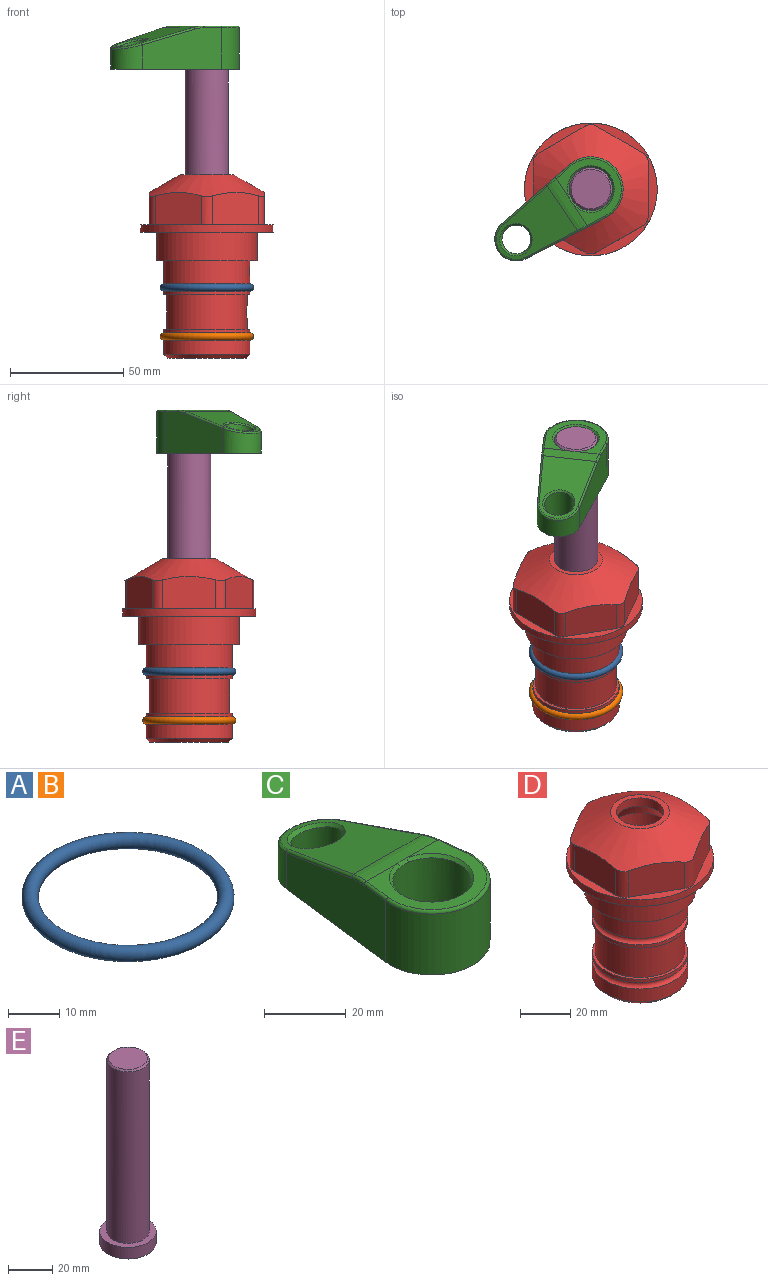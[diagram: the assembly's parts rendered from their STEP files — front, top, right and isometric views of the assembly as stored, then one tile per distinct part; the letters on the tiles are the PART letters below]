
ASSEMBLY  parts=5 mates=4
PART A: 1 faces, bbox 44.7x44.7x3.2 mm
  f0: torus R=19.05mm, axis (0,0,1), area 1193.9mm2
PART B: same geometry as A
PART C: 31 faces, bbox 31.7x65.5x19.8 mm
  f0: plane 39.12x18.26mm, normal (0.99,0.12,0), area 612.2mm2, adj f1,f4,f7,f11,f13,f15
  f1: cylinder r=9.53mm len=18.91mm, axis (0,0,-1), area 296.1mm2, adj f0,f2,f7,f17
  f2: plane 39.12x18.26mm, normal (-0.99,0.12,0), area 612.2mm2, adj f1,f4,f7,f12,f14,f16
  f3: cylinder r=6.35mm len=12.7mm, axis (0,0,-1), area 362.4mm2, adj f7,f18
  f4: cylinder r=14.29mm len=28.58mm, axis (0,0,-1), area 882.2mm2, adj f0,f2,f7,f10
  f5: cylinder r=9.53mm len=19.05mm, axis (0,0,-1), area 1092.6mm2, adj f7,f19,f20
  f6: plane 26.99x23.69mm, normal (0,0,1), area 216.2mm2, adj f9,f10,f11,f12,f19
  f7: plane 63.5x28.58mm, normal (0,0,-1), area 661.8mm2, adj f0,f1,f2,f3,f4,f5,f22,f23
  f8: plane 33.52x23.6mm, normal (0,0.26,0.97), area 486mm2, adj f9,f15,f16,f17,f18
  f9: cylinder r=19.05mm len=24.72mm, axis (1,0,0), area 120.4mm2, adj f6,f8,f13,f14,f20
  f10: torus R=13.49mm, axis (0,0,1), area 59mm2, adj f4,f6,f11,f12
  f11: cylinder r=0.79mm len=8.67mm, axis (0.12,-0.99,0), area 10.8mm2, adj f0,f6,f10,f13
  f12: cylinder r=0.79mm len=8.67mm, axis (0.12,0.99,0), area 10.8mm2, adj f2,f6,f10,f14
  f13: bspline ~4.95x1.42mm, area 6.1mm2, adj f0,f9,f11,f15
  f14: bspline ~4.95x1.42mm, area 6.1mm2, adj f2,f9,f12,f16
  f15: cylinder r=0.79mm len=25.95mm, axis (0.12,-0.96,0.26), area 32.9mm2, adj f0,f8,f13,f17
  f16: cylinder r=0.79mm len=25.95mm, axis (0.12,0.96,-0.26), area 32.9mm2, adj f2,f8,f14,f17
  f17: bspline ~18.91x8.38mm, area 30mm2, adj f1,f8,f15,f16
  f18: bspline ~14.29x14.29mm, area 48.3mm2, adj f3,f8
  f19: cone r=9.53mm half-angle=45deg, axis (0,0,1), area 66.5mm2, adj f5,f6,f20
  f20: bspline ~3.22x0.96mm, area 3.5mm2, adj f5,f9,f19
  f21: plane 2.75x2.72mm, normal (0,0,-1), area 2.9mm2, adj f23,f25,f28
  f22: plane 23.05x15.88mm, normal (-0.99,-0.12,0), area 323.6mm2, adj f7,f25,f26,f27,f28,f29
  f23: plane 23.05x15.88mm, normal (0.99,-0.12,0), area 323.6mm2, adj f7,f21,f25,f27,f28,f30
  f24: cylinder r=9.53mm len=10.69mm, axis (0,0,-1), area 114.7mm2, adj f7,f27,f29,f30
  f25: cylinder r=12.7mm len=20.59mm, axis (0,0,-1), area 381.1mm2, adj f7,f21,f22,f23,f26,f28
  f26: plane 2.75x2.72mm, normal (0,0,-1), area 2.9mm2, adj f22,f25,f28
  f27: plane 19.72x18.37mm, normal (0,-0.26,-0.97), area 291.8mm2, adj f22,f23,f24,f28,f29,f30
  f28: cylinder r=15.88mm len=19.92mm, axis (1,0,0), area 54.8mm2, adj f21,f22,f23,f25,f26,f27
  f29: cylinder r=1.59mm len=11mm, axis (0,0,-1), area 34.7mm2, adj f7,f22,f24,f27
  f30: cylinder r=1.59mm len=11mm, axis (0,0,-1), area 34.7mm2, adj f7,f23,f24,f27
PART D: 36 faces, bbox 58.7x58.7x81 mm
  f0: cylinder r=17.78mm len=35.56mm, axis (0,0,1), area 1670.8mm2, adj f23,f24,f31
  f1: cylinder r=19.05mm len=38.1mm, axis (0,0,1), area 1191.9mm2, adj f26,f27,f30
  f2: plane 58.66x58.66mm, normal (0,0,-1), area 1150.6mm2, adj f3,f28
  f3: cylinder r=29.33mm len=58.66mm, axis (0,0,-1), area 585.1mm2, adj f2,f4
  f4: plane 58.66x58.66mm, normal (0,0,1), area 475.9mm2, adj f3,f5,f6,f7,f8,f9,f10,f11
  f5: plane 20.32x14.34mm, normal (-0.5,0.87,0), area 324.4mm2, adj f4,f15,f16,f17
  f6: plane 20.32x14.34mm, normal (0.5,0.87,0), area 324.4mm2, adj f4,f14,f15,f17
  f7: plane 23.48x14.34mm, normal (1,0,0), area 324.4mm2, adj f4,f13,f14,f17
  f8: plane 20.32x14.34mm, normal (0.5,-0.87,0), area 324.4mm2, adj f4,f12,f13,f17
  f9: plane 20.32x14.34mm, normal (-0.5,-0.87,0), area 324.4mm2, adj f4,f11,f12,f17
  f10: plane 23.48x14.34mm, normal (-1,0,0), area 324.4mm2, adj f4,f11,f16,f17
  f11: cylinder r=5.08mm len=12.85mm, axis (0,0,-1), area 67.2mm2, adj f4,f9,f10,f17
  f12: cylinder r=5.08mm len=12.85mm, axis (0,0,-1), area 67.2mm2, adj f4,f8,f9,f17
  f13: cylinder r=5.08mm len=12.85mm, axis (0,0,-1), area 67.2mm2, adj f4,f7,f8,f17
  f14: cylinder r=5.08mm len=12.85mm, axis (0,0,-1), area 67.2mm2, adj f4,f6,f7,f17
  f15: cylinder r=5.08mm len=12.85mm, axis (0,0,-1), area 67.2mm2, adj f4,f5,f6,f17
  f16: cylinder r=5.08mm len=12.85mm, axis (0,0,-1), area 67.2mm2, adj f4,f5,f10,f17
  f17: cone r=11.73mm half-angle=60deg, axis (0,0,-1), area 2071.8mm2, adj f5,f6,f7,f8,f9,f10,f11,f12
  f18: plane 23.46x23.46mm, normal (0,0,1), area 147.4mm2, adj f17,f35
  f19: plane 34.93x34.93mm, normal (0,0,-1), area 958mm2, adj f29
  f20: cylinder r=19.05mm len=38.1mm, axis (0,0,1), area 760.1mm2, adj f21,f29
  f21: torus R=19.05mm, axis (0,0,1), area 565.3mm2, adj f20,f22
  f22: cylinder r=19.05mm len=38.1mm, axis (0,0,1), area 190mm2, adj f21,f23
  f23: plane 38.1x38.1mm, normal (0,0,1), area 146.9mm2, adj f0,f22
  f24: plane 38.1x38.1mm, normal (0,0,-1), area 146.9mm2, adj f0,f25
  f25: cylinder r=19.05mm len=38.1mm, axis (0,0,1), area 190mm2, adj f24,f26
  f26: torus R=19.05mm, axis (0,0,1), area 565.3mm2, adj f1,f25
  f27: plane 44.45x44.45mm, normal (0,0,-1), area 411.7mm2, adj f1,f28
  f28: cylinder r=22.23mm len=44.45mm, axis (0,0,1), area 1773.5mm2, adj f2,f27
  f29: cone r=19.05mm half-angle=45deg, axis (0,0,1), area 257.5mm2, adj f19,f20
  f30: cylinder r=3.17mm len=6.75mm, axis (-1,0,0), area 128mm2, adj f1,f33
  f31: cylinder r=3.17mm len=6.35mm, axis (-1,0,0), area 102.5mm2, adj f0,f33
  f32: plane 25.4x25.4mm, normal (0,0,1), area 506.7mm2, adj f33
  f33: cylinder r=12.7mm len=66.42mm, axis (0,0,-1), area 5236.2mm2, adj f30,f31,f32,f34
  f34: cone r=9.53mm half-angle=30deg, axis (0,0,-1), area 443.4mm2, adj f33,f35
  f35: cylinder r=9.53mm len=19.05mm, axis (0,0,-1), area 240.9mm2, adj f18,f34
PART E: 6 faces, bbox 25.4x25.4x101.6 mm
  f0: plane 17.46x17.46mm, normal (0,0,1), area 239.5mm2, adj f5
  f1: plane 25.4x25.4mm, normal (0,0,-1), area 506.7mm2, adj f2
  f2: cylinder r=12.7mm len=25.4mm, axis (0,0,1), area 506.7mm2, adj f1,f3
  f3: plane 25.4x25.4mm, normal (0,0,1), area 221.7mm2, adj f2,f4
  f4: cylinder r=9.53mm len=94.46mm, axis (0,0,1), area 5653mm2, adj f3,f5
  f5: cone r=8.73mm half-angle=45deg, axis (0,0,-1), area 64.4mm2, adj f0,f4
PLACE A at identity
PLACE B t=(0,0,-21.59)mm
PLACE C rot(axis=(0,0,1),124deg) t=(0,0,27.55)mm
PLACE D at identity fixed
PLACE E rot(axis=(0,0,1),124deg) t=(0,0,27.55)mm
MATE fastened A.f0 <-> D.f0  axis (0,0,1) through (0,0,-24.51)mm
MATE fastened B.f0 <-> D.f0  axis (0,0,1) through (0,0,-46.1)mm
MATE fastened C.f4 <-> E.f2  axis (0,0,1) through (0,0,91.05)mm
MATE cylindrical E.f2 <-> D.f0  axis (0,0,-1) through (0,0,-10.55)mm
